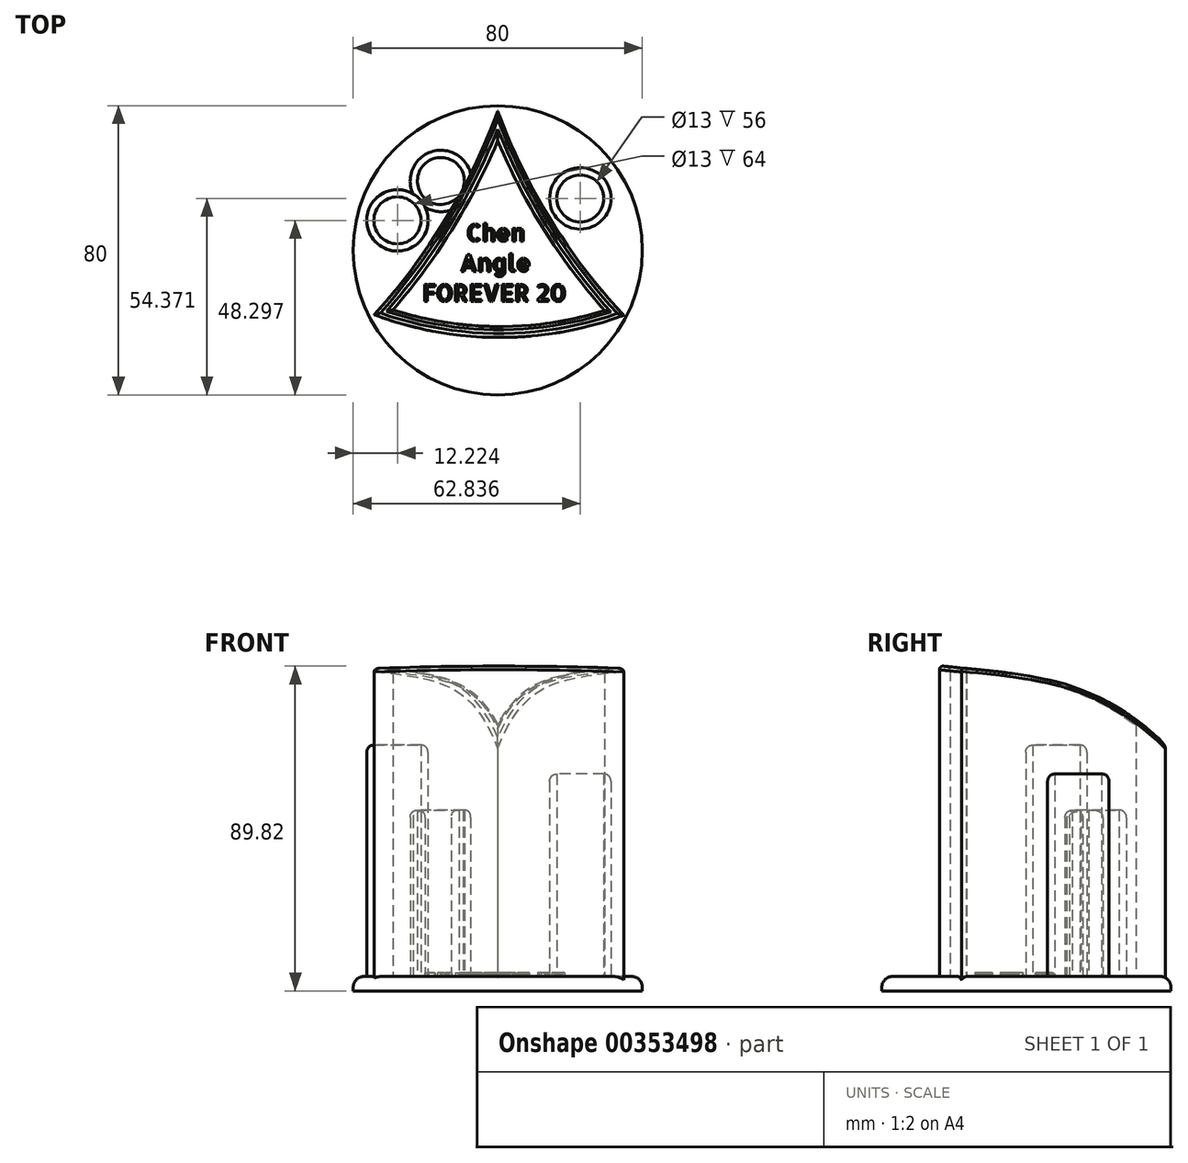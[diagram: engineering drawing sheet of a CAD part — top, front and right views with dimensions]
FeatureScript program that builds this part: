
annotation { "Feature Type Name" : "Feature", "Feature Type Description" : "" }
export const myFeature = defineFeature(function(context is Context, id is Id, definition is map)
    precondition{}
    {
        {
            var Q0;
            Q0=qCreatedBy(makeId("Top.planeOp"),FACE);
            var sketch = newSketch(context, id + "F0", { "sketchPlane" : qUnion([Q0])});
            skCircle(sketch, "E0", {"center": v(0, 0) * mm, "radius": 40 * mm});
            skSolve(sketch);
        }
        {
            var Q0;
            Q0 = qSketchRegion(id + "F0", true);
            extrude(context, id + "F1", {"entities" : qUnion([Q0]), "depth" : 4 * mm});
        }
        {
            var Q0;
            Q0=makeQuery(id+"F1.opExtrude","CAP_EDGE",EDGE,{"disambiguationData":[OSD([sQuery(id+"F0.wireOp",EDGE,"E0")])],"isStart":false});
            fillet(context, id + "F2", {"entities" : qUnion([Q0]), "radius" : 3 * mm, "tangentPropagation" : true, "allowEdgeOverflow" : false});
        }
        {
            var Q0;
            Q0=qCreatedBy(makeId("Top.planeOp"),FACE);
            var sketch = newSketch(context, id + "F3", { "sketchPlane" : qUnion([Q0])});
            skArc(sketch, "E1", {"start": v(-34.22, -17.84) * mm, "mid": v(0.3, -24.08) * mm, "end": v(34.83, -17.98) * mm});
            skArc(sketch, "E2", {"start": v(-34.22, -17.84) * mm, "mid": v(-14.4, 8.67) * mm, "end": v(0, 38.47) * mm});
            skArc(sketch, "E3", {"start": v(0, 38.47) * mm, "mid": v(14.6, 8.5) * mm, "end": v(34.83, -17.98) * mm});
            skArc(sketch, "E4.0", {"start": v(-29, -16.47) * mm, "mid": v(-12.66, 5.78) * mm, "end": v(0, 30.3) * mm});
            skArc(sketch, "E4.1", {"start": v(-29, -16.47) * mm, "mid": v(0.25, -21.08) * mm, "end": v(29.53, -16.62) * mm});
            skArc(sketch, "E4.2", {"start": v(0, 30.3) * mm, "mid": v(12.84, 5.63) * mm, "end": v(29.53, -16.62) * mm});
            skSolve(sketch);
        }
        {
            var Q0;
            Q0 = qSketchRegion(id + "F3", true);
            extrude(context, id + "F4", {"entities" : qUnion([Q0]), "operationType" : NewBodyOperationType.ADD, "depth" : 90 * mm});
        }
        {
            var Q0;
            Q0=qCreatedBy(makeId("Right.planeOp"),FACE);
            var sketch = newSketch(context, id + "F5", { "sketchPlane" : qUnion([Q0])});
            skFitSpline(sketch, "E5", {"points": [v(-48.2, 100.38) * mm, v(-37.5, 92.84) * mm, v(12.13, 84.39) * mm, v(49.78, 55.73) * mm], "startDerivative": vector(67.27, -23.57) * mm, "endDerivative": vector(70.32, -86.12) * mm});
            skLineSegment(sketch, "E6", {"start": v(-48.2, 100.38) * mm, "end": v(13.48, 116.92) * mm});
            skLineSegment(sketch, "E7", {"start": v(13.48, 116.92) * mm, "end": v(73.98, 100.38) * mm});
            skLineSegment(sketch, "E8", {"start": v(73.98, 100.38) * mm, "end": v(49.78, 55.73) * mm});
            skSolve(sketch);
        }
        {
            var Q0;
            Q0 = qSketchRegion(id + "F5", true);
            extrude(context, id + "F6", {"entities" : qUnion([Q0]), "operationType" : NewBodyOperationType.REMOVE, "oppositeDirection" : true, "depth" : 54.6 * mm, "hasSecondDirection" : true, "secondDirectionOppositeDirection" : false, "secondDirectionDepth" : 60.7 * mm});
        }
        {
            var Q0;
            Q0=makeQuery(id+"F6.boolean.opBoolean","COPY",FACE,{"derivedFrom":makeQuery(id+"F6.opExtrude","SWEPT_FACE",FACE,{"disambiguationData":[OSD([sQuery(id+"F5.wireOp",EDGE,"E5")])]})});
            fillet(context, id + "F7", {"entities" : qUnion([Q0]), "radius" : 1 * mm, "tangentPropagation" : true, "allowEdgeOverflow" : false});
        }
        {
            var Q0;
            Q0=qCreatedBy(makeId("Top.planeOp"),FACE);
            var sketch = newSketch(context, id + "F8", { "sketchPlane" : qUnion([Q0])});
            skText(sketch, "E9", { "text": "       Chen \n      Angle\nFOREVER 20", "fontName": "AllertaStencil-Regular.ttf"});
            const initialGuessF8  = {"E9": [-0.02089, 0.0025, 1, 0, 0.00468]};
            skSetInitialGuess(sketch, initialGuessF8);
            skSolve(sketch);
        }
        {
            var Q0;
            Q0 = qSketchRegion(id + "F8", true);
            extrude(context, id + "F9", {"entities" : qUnion([Q0]), "operationType" : NewBodyOperationType.ADD, "depth" : 5 * mm});
        }
        {
            var Q0;
            Q0=qCreatedBy(makeId("Top.planeOp"),FACE);
            var sketch = newSketch(context, id + "F10", { "sketchPlane" : qUnion([Q0])});
            skCircle(sketch, "E10", {"center": v(22.84, 14.37) * mm, "radius": 6.5 * mm});
            skCircle(sketch, "E11.0", {"center": v(22.84, 14.37) * mm, "radius": 8.5 * mm});
            skSolve(sketch);
        }
        {
            var Q0;
            Q0 = qSketchRegion(id + "F10", true);
            extrude(context, id + "F11", {"entities" : qUnion([Q0]), "operationType" : NewBodyOperationType.ADD, "depth" : 60 * mm});
        }
        {
            var Q0;
            Q0=makeQuery(id+"F11.opExtrude","CAP_EDGE",EDGE,{"disambiguationData":[OSD([sQuery(id+"F10.wireOp",EDGE,"E11.0")])],"isStart":false});
            fillet(context, id + "F12", {"entities" : qUnion([Q0]), "radius" : 2 * mm, "tangentPropagation" : true, "allowEdgeOverflow" : false});
        }
        {
            var Q0;
            Q0=qCreatedBy(makeId("Top.planeOp"),FACE);
            var sketch = newSketch(context, id + "F13", { "sketchPlane" : qUnion([Q0])});
            skCircle(sketch, "E12", {"center": v(-15.74, 19.19) * mm, "radius": 6.5 * mm});
            skCircle(sketch, "E13.0", {"center": v(-15.74, 19.19) * mm, "radius": 8.5 * mm});
            skSolve(sketch);
        }
        {
            var Q0;
            Q0 = qSketchRegion(id + "F13", true);
            extrude(context, id + "F14", {"entities" : qUnion([Q0]), "operationType" : NewBodyOperationType.ADD, "depth" : 50 * mm});
        }
        {
            var Q0;
            Q0=qCreatedBy(makeId("Top.planeOp"),FACE);
            var sketch = newSketch(context, id + "F15", { "sketchPlane" : qUnion([Q0])});
            skCircle(sketch, "E14", {"center": v(-27.78, 8.3) * mm, "radius": 6.5 * mm});
            skCircle(sketch, "E15.0", {"center": v(-27.78, 8.3) * mm, "radius": 8.5 * mm});
            skSolve(sketch);
        }
        {
            var Q0;
            Q0 = qSketchRegion(id + "F15", true);
            extrude(context, id + "F16", {"entities" : qUnion([Q0]), "operationType" : NewBodyOperationType.ADD, "depth" : 68 * mm});
        }
        {
            var Q0;
            Q0=makeQuery(id+"F16.opExtrude","CAP_EDGE",EDGE,{"disambiguationData":[OSD([sQuery(id+"F15.wireOp",EDGE,"E15.0")])],"isStart":false});
            var Q1;
            Q1=makeQuery(id+"F16.boolean.opBoolean","SPLIT",EDGE,{"disambiguationData":[OD(1.0)],"derivedFrom":makeQuery(id+"F14.opExtrude","CAP_EDGE",EDGE,{"disambiguationData":[OSD([sQuery(id+"F13.wireOp",EDGE,"E13.0")])],"isStart":false})});
            var Q2;
            Q2=makeQuery(id+"F16.boolean.opBoolean","SPLIT",EDGE,{"disambiguationData":[OD(0.0)],"derivedFrom":makeQuery(id+"F14.opExtrude","CAP_EDGE",EDGE,{"disambiguationData":[OSD([sQuery(id+"F13.wireOp",EDGE,"E13.0")])],"isStart":false})});
            fillet(context, id + "F17", {"entities" : qUnion([Q0, Q1, Q2]), "radius" : 2 * mm, "tangentPropagation" : true, "allowEdgeOverflow" : false});
        }
    });
